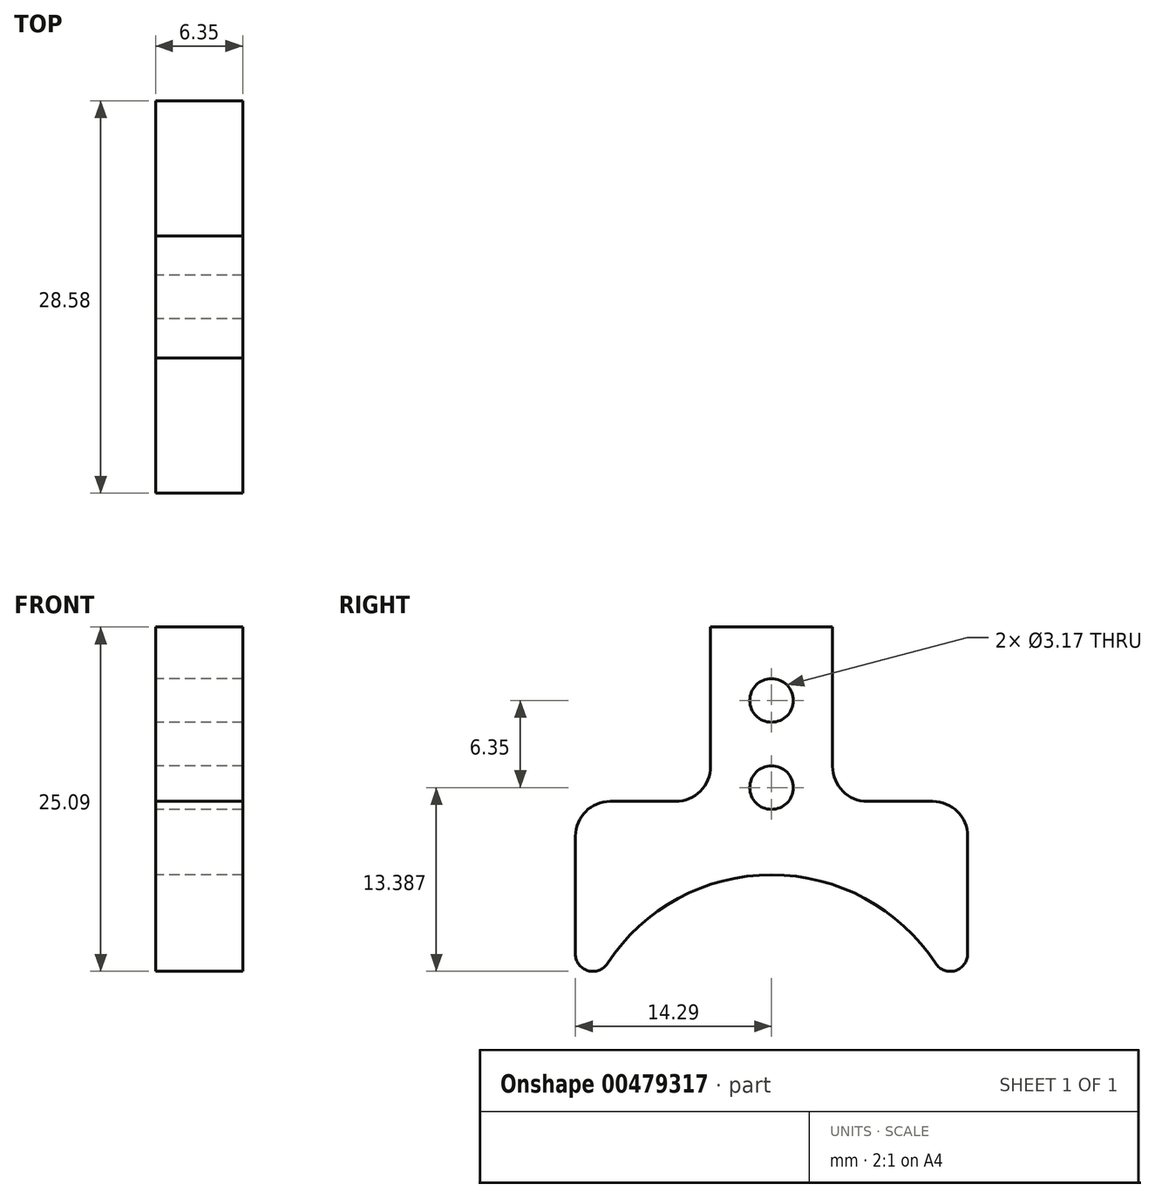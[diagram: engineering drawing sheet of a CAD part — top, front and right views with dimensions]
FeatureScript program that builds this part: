
annotation { "Feature Type Name" : "Feature", "Feature Type Description" : "" }
export const myFeature = defineFeature(function(context is Context, id is Id, definition is map)
    precondition{}
    {
        {
            var Q0;
            Q0=qCreatedBy(makeId("Right.planeOp"),FACE);
            var sketch = newSketch(context, id + "F0", { "sketchPlane" : qUnion([Q0])});
            skLineSegment(sketch, "E0.bottom", {"start": v(-29.39, 0) * mm, "end": v(11.89, 0) * mm});
            skLineSegment(sketch, "E1", {"start": v(-23.04, 0) * mm, "end": v(-23.04, 44.45) * mm, "construction": true});
            skLineSegment(sketch, "E2", {"start": v(5.54, 0) * mm, "end": v(5.54, 44.45) * mm, "construction": true});
            skArc(sketch, "E3", {"start": v(5.54, 0) * mm, "mid": v(-8.75, 14.29) * mm, "end": v(-23.04, 0) * mm});
            skLineSegment(sketch, "E4", {"start": v(-8.75, 0) * mm, "end": v(-8.75, 46.64) * mm, "construction": true});
            skCircle(sketch, "E5", {"center": v(-8.75, 20.64) * mm, "radius": 1.59 * mm});
            skLineSegment(sketch, "E6", {"start": v(-13.2, 19.64) * mm, "end": v(-13.2, 32.34) * mm});
            skLineSegment(sketch, "E7.MirrorCS", {"start": v(-4.3, 19.64) * mm, "end": v(-4.3, 32.34) * mm});
            skLineSegment(sketch, "E8", {"start": v(-13.2, 32.34) * mm, "end": v(-4.3, 32.34) * mm});
            skLineSegment(sketch, "E9", {"start": v(-8.75, 0) * mm, "end": v(-8.75, 88.26) * mm, "construction": true});
            skCircle(sketch, "E10", {"center": v(-8.75, 26.99) * mm, "radius": 1.59 * mm});
            skLineSegment(sketch, "E11", {"start": v(-4.3, 19.64) * mm, "end": v(-44.13, 19.64) * mm, "construction": true});
            skLineSegment(sketch, "E12", {"start": v(-4.3, 19.64) * mm, "end": v(27.26, 19.64) * mm, "construction": true});
            skLineSegment(sketch, "E13", {"start": v(-23.04, 0) * mm, "end": v(-23.04, 19.64) * mm});
            skPoint(sketch, "E13.endSnap0", {"position": v(-24.22, 19.64) * mm});
            skLineSegment(sketch, "E14", {"start": v(-23.04, 19.64) * mm, "end": v(-13.2, 19.64) * mm});
            skLineSegment(sketch, "E15", {"start": v(5.54, 0) * mm, "end": v(5.54, 19.64) * mm});
            skLineSegment(sketch, "E16", {"start": v(5.54, 19.64) * mm, "end": v(-4.3, 19.64) * mm});
            skSolve(sketch);
        }
        {
            var Q0;
            Q0=makeQuery(id+"F0.imprint","IMPRINT",FACE,{"disambiguationData":[TD([[makeQuery(id+"F0.imprint","IMPRINT",EDGE,{"derivedFrom":sQuery(id+"F0.wireOp",EDGE,"E0.top")}),-1.0]])]});
            var Q1;
            {var subQ4=sQuery(id+"F0.wireOp",EDGE,"E3");Q1=makeQuery(id+"F0.imprint","IMPRINT",FACE,{"disambiguationData":[TD([[makeQuery(id+"F0.imprint","IMPRINT",EDGE,{"derivedFrom":subQ4}),-1.0]])]});}
            var Q2;
            {var subQ2=sQuery(id+"F0.wireOp",EDGE,"E5");Q2=makeQuery(id+"F0.imprint","IMPRINT",FACE,{"disambiguationData":[TD([[makeQuery(id+"F0.imprint","IMPRINT",EDGE,{"derivedFrom":subQ2}),-1.0]])]});}
            var Q3;
            {var subQ1=sQuery(id+"F0.wireOp",EDGE,"E6");Q3=makeQuery(id+"F0.imprint","IMPRINT",FACE,{"disambiguationData":[TD([[makeQuery(id+"F0.imprint","IMPRINT",EDGE,{"derivedFrom":subQ1}),-1.0]])]});}
            extrude(context, id + "F1", {"entities" : qUnion([Q0, Q1, Q2, Q3]), "depth" : 6.35 * mm});
        }
        {
            var Q0;
            Q0=makeQuery(id+"F1.opExtrude","SWEPT_EDGE",EDGE,{"disambiguationData":[OSD([sQuery(id+"F0.wireOp",EDGE,"E0.bottom"),sQuery(id+"F0.wireOp",EDGE,"E3"),sQuery(id+"F0.wireOp",EDGE,"E13")])]});
            var Q1;
            Q1=makeQuery(id+"F1.opExtrude","SWEPT_EDGE",EDGE,{"disambiguationData":[OSD([sQuery(id+"F0.wireOp",EDGE,"E0.bottom"),sQuery(id+"F0.wireOp",EDGE,"E3"),sQuery(id+"F0.wireOp",EDGE,"E15")])]});
            fillet(context, id + "F2", {"entities" : qUnion([Q0, Q1]), "radius" : 1.27 * mm, "tangentPropagation" : true, "allowEdgeOverflow" : false});
        }
        {
            var Q0;
            Q0=makeQuery(id+"F1.opExtrude","SWEPT_EDGE",EDGE,{"disambiguationData":[OSD([sQuery(id+"F0.wireOp",EDGE,"E13"),sQuery(id+"F0.wireOp",EDGE,"E14")])]});
            var Q1;
            Q1=makeQuery(id+"F1.opExtrude","SWEPT_EDGE",EDGE,{"disambiguationData":[OSD([sQuery(id+"F0.wireOp",EDGE,"E15"),sQuery(id+"F0.wireOp",EDGE,"E16")])]});
            var Q2;
            Q2=makeQuery(id+"F1.opExtrude","SWEPT_EDGE",EDGE,{"disambiguationData":[OSD([sQuery(id+"F0.wireOp",EDGE,"E7.MirrorCS"),sQuery(id+"F0.wireOp",EDGE,"E16")])]});
            var Q3;
            Q3=makeQuery(id+"F1.opExtrude","SWEPT_EDGE",EDGE,{"disambiguationData":[OSD([sQuery(id+"F0.wireOp",EDGE,"E6"),sQuery(id+"F0.wireOp",EDGE,"E14")])]});
            fillet(context, id + "F3", {"entities" : qUnion([Q0, Q1, Q2, Q3]), "radius" : 2.54 * mm, "tangentPropagation" : true, "allowEdgeOverflow" : false});
        }
    });
